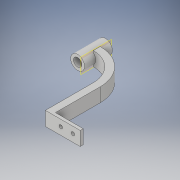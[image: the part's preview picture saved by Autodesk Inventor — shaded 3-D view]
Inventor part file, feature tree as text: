
AUTODESK INVENTOR PART (.ipt)
format: ipt  version: 2019 (Build 230136000, 136)  size: 145,920 bytes
history: native  units: in
note: dims shown in document units (in); Inventor stores cm internally (conversion verified against a paired STEP export)
features: sketch x7, extrude x3, hole x1, plane x1, sweep x1
ambient origin geometry x8: Origin, YZ Plane, XZ Plane, XY Plane, X Axis, Y Axis, Z Axis, Center Point
bodies: Solid1 (feature_tree)
feature tree (13):
  sketch  "Sketch1"  dims[d1=0.5in d2=0.0in]
  extrude  "Extrusion1"  Depth=0.125in
  hole  "Hole1"  [1 undecoded]
  plane  "Work Plane1"
  sweep  "Sweep1"
  extrude  "Extrusion2"  TaperAngle=0.0deg  [1 undecoded]
  extrude  "Extrusion3"  Depth=0.5in TaperAngle=0.0deg
  sketch  "Sketch2"  dims[d3=0.15in d4=0.75in d5=0.375in d6=0.25in d7=0.5635in d8=1.0in d9=0.8108in d10=0.125in]
  sketch  "Sketch3"  dims[d11=0.125in d12=0.2in]
  sketch  "Sketch4"  dims[d13=0.5in d14=0.2in]
  sketch  "Sketch5"  dims[d15=0.0in d16=0.0in d17=0.0in]
  sketch  "Sketch6"  dims[d18=0.5in d19=0.0in d28=0.5in d29=0.0in]
  sketch  "Sketch7"
note: 2 required parameter values undecoded (feature->parameter linkage not recoverable at this tier; creation-order binding heuristic only, values carry confidence <= 0.55)
